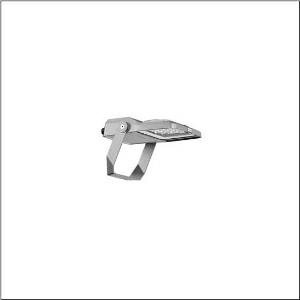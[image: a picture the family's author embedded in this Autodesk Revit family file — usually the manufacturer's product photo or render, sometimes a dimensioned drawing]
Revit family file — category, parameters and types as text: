
# Revit family: floodlight_fl_21_micro___rsd12_5xa7762a4b1a_7da4
name_source: partatom
category: Lighting Fixtures
units: mm (PartAtom-declared; Revit-internal decimal feet)

## family parameters
Cut with Voids When Loaded = No
Host = Face
Light Source = No
Part Type = Normal
Room Calculation Point = No
Round Connector Dimension = Use Diameter
Shared = No

## types (1)
- --- (1 x LED, 3220 lm, 23.1 W, 4000K)
    Apparent Load = 23 VA
    CIE Flux Codes = 79 92 99 100 100
    Color Rendering = 70
    Color Temperature = 4000K
    Default Elevation = 1800 mm
    Description = Floodlight FL 21 micro, floodlight, primary light control with lens, of PMMA, primary optical cover: protective disc, of toughened safety glass, transparent, light distribution: RSD12, light emission: direct distribution, installation type: surface-mounted, LED, High Power LED, rated luminous flux: 3.220lm, luminous efficacy: 139lm/W, light colour: 740, colour temperature: 4000K, control gear: ECG iQ, control: Auto-Match, Temp-Guard, Night-Set, Smart-Wire, Desk-Remote (wireless, voltage-free reading and setting of iQ features in the workshop via application-optimized NFC function/RFID function), optimised constant luminous flux control (CLO 2.0), Street-Remote, with terminal, 6-pole, mains connection: 220..240V, AC, 50/60Hz, start of lifetime: 23W, end of lifetime: 24W, reduction: 11W, luminaire housing, of diecast aluminium, powder-coated, Siteco® metallic grey (DB 702S), corrosivity category C5 according to DIN EN ISO 12944, mounting bracket, of steel, galvanised, powder-coated, Siteco® metallic grey (DB 702S), protection rating (complete): IP66, insulation class (complete): insulation class II (safety insulation), certification: CE, protection symbol: D, impact resistance: IK07, permissible operating ambient temperature: -40..+40°C, permissible operating ambient temperature for outdoor applications: -40..+50°C, standard: DIN EN 12944, packaging unit: 1 piece

Light Distribution: RSD12
    Height = 65 mm
    Lamp = 1 x LED
    Lamp Light Flux = 3220 lm
    Lamp Power = 23.1 W
    Lamp count = 1
    Length = 312 mm
    Luminous efficacy = 139 lm/W
    Manufacturer = Siteco
    ModVariant = No
    Model = 5XA7762A4B1A
    Number of Poles = 1
    OnlyDefault = Yes
    Power Factor = 1
    Product Name = Floodlight FL 21 micro | RSD12
    Product group = floodlight | pylon top
    ProductGroupID = 6101
    Protection Class = Protection class II
    Protection Degree = IP 66
    RLX_Detail_Level = 1
    RlxData = <blob elided: 74869 chars, md5=e71c6ba6>
    Socket = socket
    Standby Power = 0 W
    System Light Flux = 3220 lm
    System Power = 23 W
    Type Comments = factory setting: luminous flux: 100 % | dim-lin: 254 | 455 mA
    Type Image = l_1006880.jpg
    URL = http://relux.com
    VarID = @adj_095427
    Voltage = 0 V
    Weight = 0.00 kg
    Width = 230 mm

## geometry (parser evidence)
native form markers: Blend x4, Sweep x12
no freeform markers — native parametric forms only
